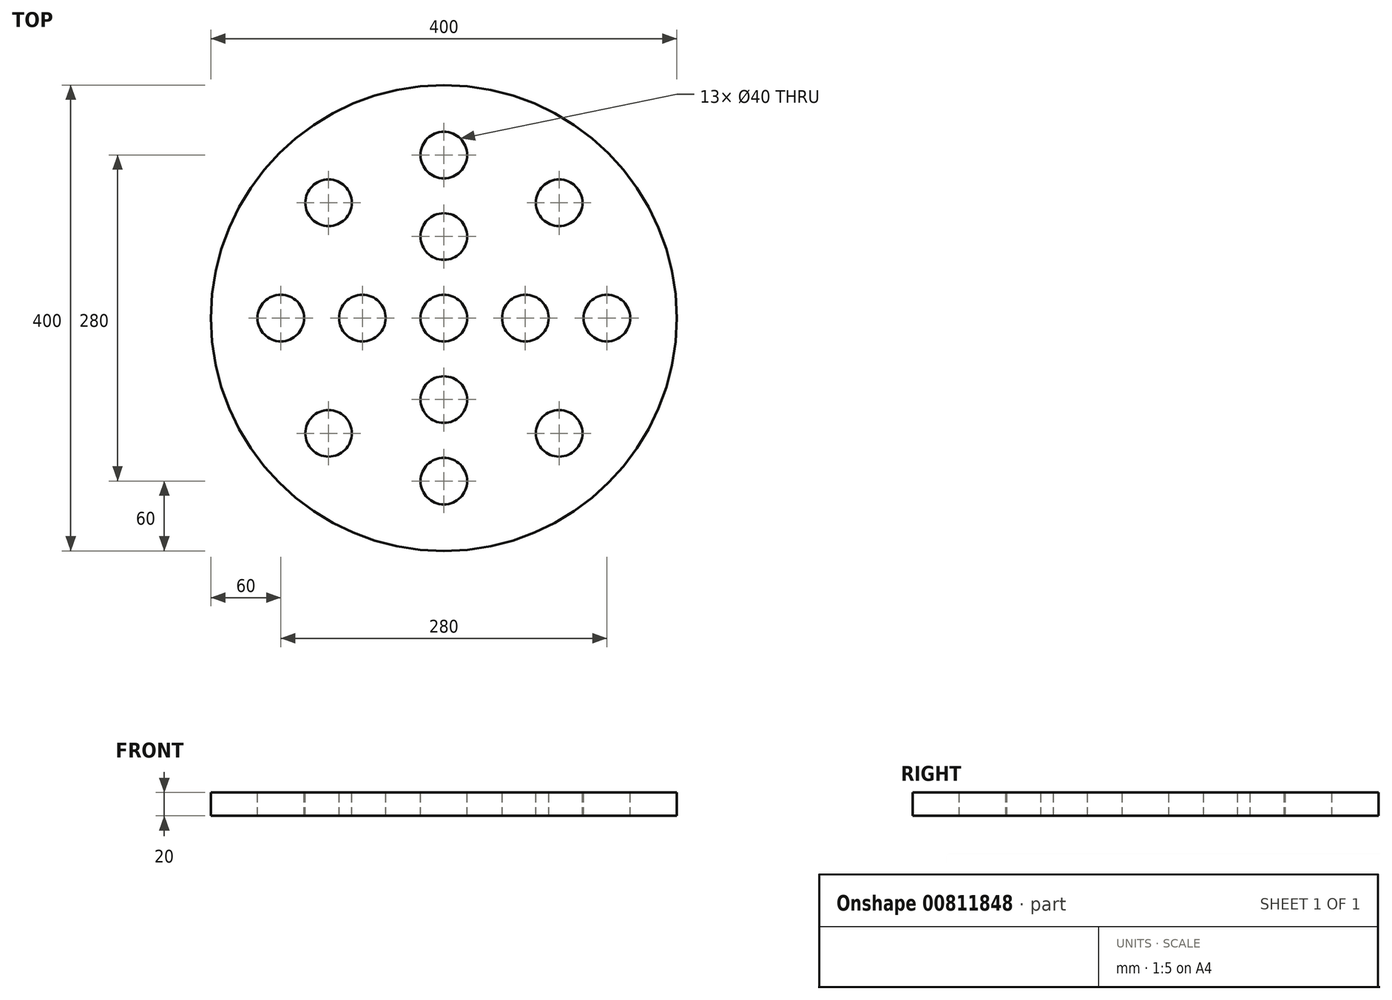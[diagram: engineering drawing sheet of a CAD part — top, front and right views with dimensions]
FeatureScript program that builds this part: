
annotation { "Feature Type Name" : "Feature", "Feature Type Description" : "" }
export const myFeature = defineFeature(function(context is Context, id is Id, definition is map)
    precondition{}
    {
        {
            var Q0;
            Q0=qCreatedBy(makeId("Top.planeOp"),FACE);
            var sketch = newSketch(context, id + "F0", { "sketchPlane" : qUnion([Q0])});
            skCircle(sketch, "E0", {"center": v(0, 0) * mm, "radius": 200 * mm});
            skSolve(sketch);
        }
        {
            var Q0;
            Q0 = qSketchRegion(id + "F0", true);
            extrude(context, id + "F1", {"entities" : qUnion([Q0]), "depth" : 20 * mm, "offsetDistance" : 25 * mm});
        }
        {
            var Q0;
            Q0=makeQuery(id+"F1.opExtrude","CAP_FACE",FACE,{"disambiguationData":[OSD([sQuery(id+"F0.wireOp",EDGE,"E0")])],"isStart":false});
            var sketch = newSketch(context, id + "F2", { "sketchPlane" : qUnion([Q0])});
            skCircle(sketch, "E1", {"center": v(0, 0) * mm, "radius": 20 * mm});
            skCircle(sketch, "E2", {"center": v(-70, 0) * mm, "radius": 20 * mm});
            skCircle(sketch, "E3", {"center": v(-140, 0) * mm, "radius": 20 * mm});
            skCircle(sketch, "E4.1.0", {"center": v(0, -70) * mm, "radius": 20 * mm});
            skCircle(sketch, "E4.2.0", {"center": v(70, 0) * mm, "radius": 20 * mm});
            skCircle(sketch, "E4.3.0", {"center": v(0, 70) * mm, "radius": 20 * mm});
            skCircle(sketch, "E5.1.0", {"center": v(-99, -99) * mm, "radius": 20 * mm});
            skCircle(sketch, "E5.2.0", {"center": v(0, -140) * mm, "radius": 20 * mm});
            skCircle(sketch, "E5.3.0", {"center": v(99, -99) * mm, "radius": 20 * mm});
            skCircle(sketch, "E5.4.0", {"center": v(140, 0) * mm, "radius": 20 * mm});
            skCircle(sketch, "E5.5.0", {"center": v(99, 99) * mm, "radius": 20 * mm});
            skCircle(sketch, "E5.6.0", {"center": v(0, 140) * mm, "radius": 20 * mm});
            skCircle(sketch, "E5.7.0", {"center": v(-99, 99) * mm, "radius": 20 * mm});
            skSolve(sketch);
        }
        {
            var Q0;
            Q0 = qSketchRegion(id + "F2", true);
            extrude(context, id + "F3", {"entities" : qUnion([Q0]), "operationType" : NewBodyOperationType.REMOVE, "oppositeDirection" : true, "depth" : 25 * mm, "offsetDistance" : 25 * mm});
        }
    });
